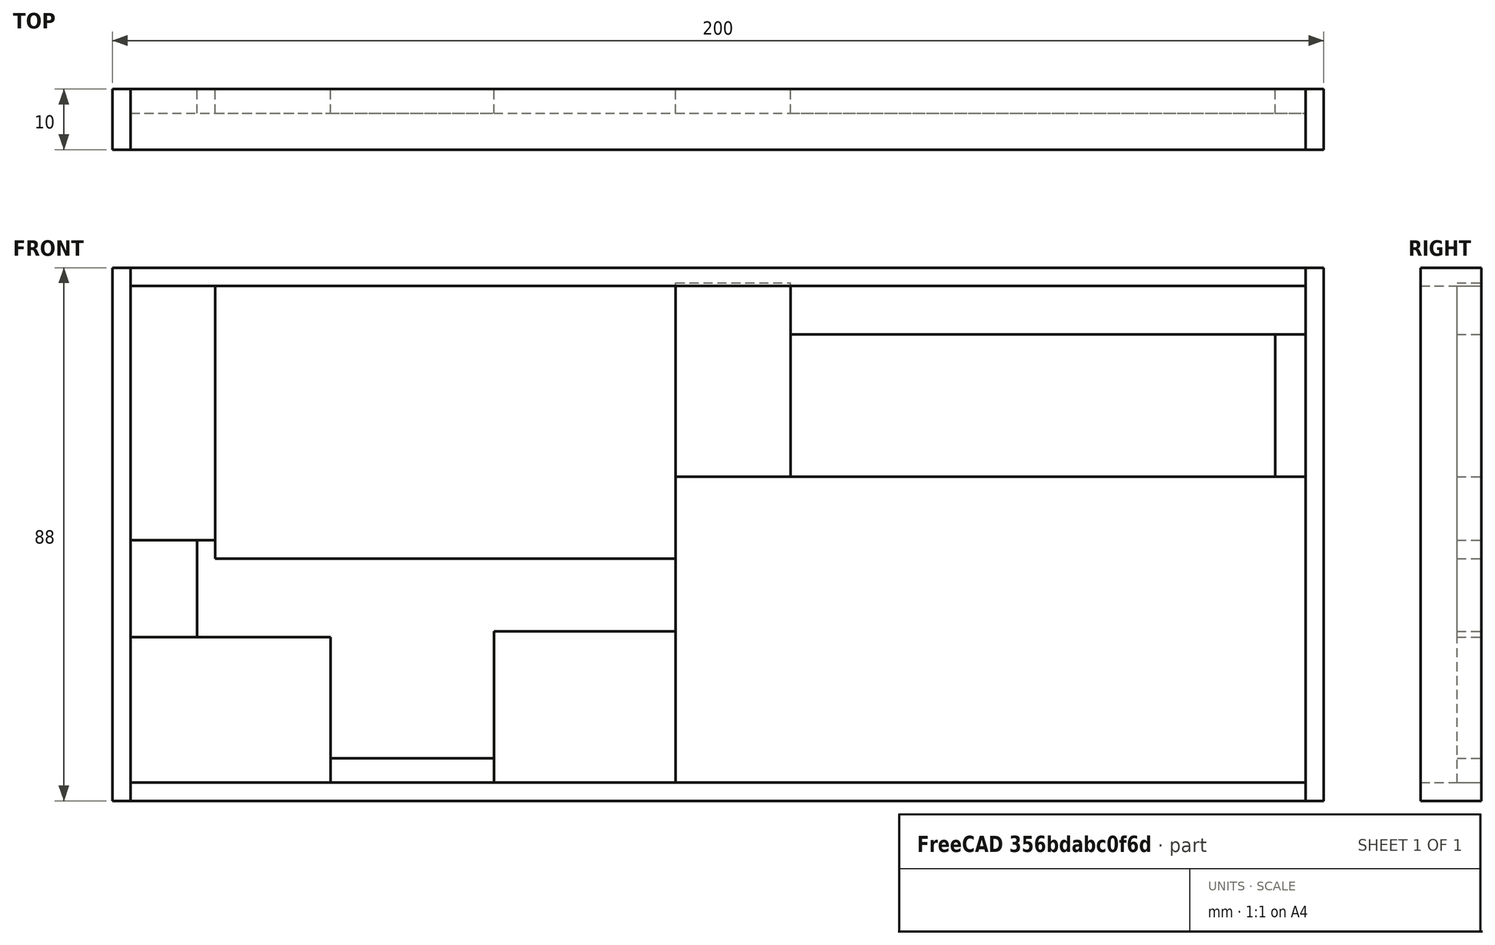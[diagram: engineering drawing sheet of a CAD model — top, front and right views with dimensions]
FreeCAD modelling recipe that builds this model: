
FCSTD DOCUMENT  (FreeCAD 0.15R4671 (Git))
Label: lcd breadboard case - lid 2
License: All rights reserved
LicenseURL: http://en.wikipedia.org/wiki/All_rights_reserved
objects: Part::Box×14
note: 14 computed .brp shape members not serialized (recipe doc carries the construction recipe); baked Part::Feature solids carry a one-line shape summary decoded from their .brp

FEATURE [Part::Box] Box  label="side 001"
  Height = 88
  Length = 3
  Width = 10
FEATURE [Part::Box] Box001  label="side 002"
  Height = 3
  Length = 194
  Placement = pos=(3,0,0) rot=(0,0,1;0rad)
  Width = 10
FEATURE [Part::Box] Box002  label="side 003"
  Height = 88
  Length = 3
  Placement = pos=(197,0,0) rot=(0,0,1;0rad)
  Width = 10
FEATURE [Part::Box] Box003  label="side 004"
  Height = 3
  Length = 194
  Placement = pos=(3,0,85) rot=(0,0,1;0rad)
  Width = 10
FEATURE [Part::Box] Box004  label="cover 001"
  Height = 50.5
  Length = 104
  Placement = pos=(93,6,3) rot=(0,0,1;0rad)
  Width = 4
FEATURE [Part::Box] Box005  label="cover 002"
  Height = 23.5
  Length = 5
  Placement = pos=(192,6,53.5) rot=(0,0,1;0rad)
  Width = 4
FEATURE [Part::Box] Box006  label="cover 003"
  Height = 8
  Length = 85
  Placement = pos=(112,6,77) rot=(0,0,1;0rad)
  Width = 4
FEATURE [Part::Box] Box007  label="cover 004"
  Height = 32
  Length = 19
  Placement = pos=(93,6,53.5) rot=(0,0,1;0rad)
  Width = 4
FEATURE [Part::Box] Box009  label="cover 005"
  Height = 45
  Length = 76
  Placement = pos=(17,6,40) rot=(0,0,1;0rad)
  Width = 4
FEATURE [Part::Box] Box010  label="cover 006"
  Height = 25
  Length = 30
  Placement = pos=(63,6,3) rot=(0,0,1;0rad)
  Width = 4
FEATURE [Part::Box] Box011  label="cover 007"
  Height = 4
  Length = 27
  Placement = pos=(36,6,3) rot=(0,0,1;0rad)
  Width = 4
FEATURE [Part::Box] Box012  label="cover 008"
  Height = 24
  Length = 33
  Placement = pos=(3,6,3) rot=(0,0,1;0rad)
  Width = 4
FEATURE [Part::Box] Box013  label="cover 009"
  Height = 42
  Length = 14
  Placement = pos=(3,6,43) rot=(0,0,1;0rad)
  Width = 4
FEATURE [Part::Box] Box014  label="cover 010"
  Height = 16
  Length = 11
  Placement = pos=(3,6,27) rot=(0,0,1;0rad)
  Width = 4
